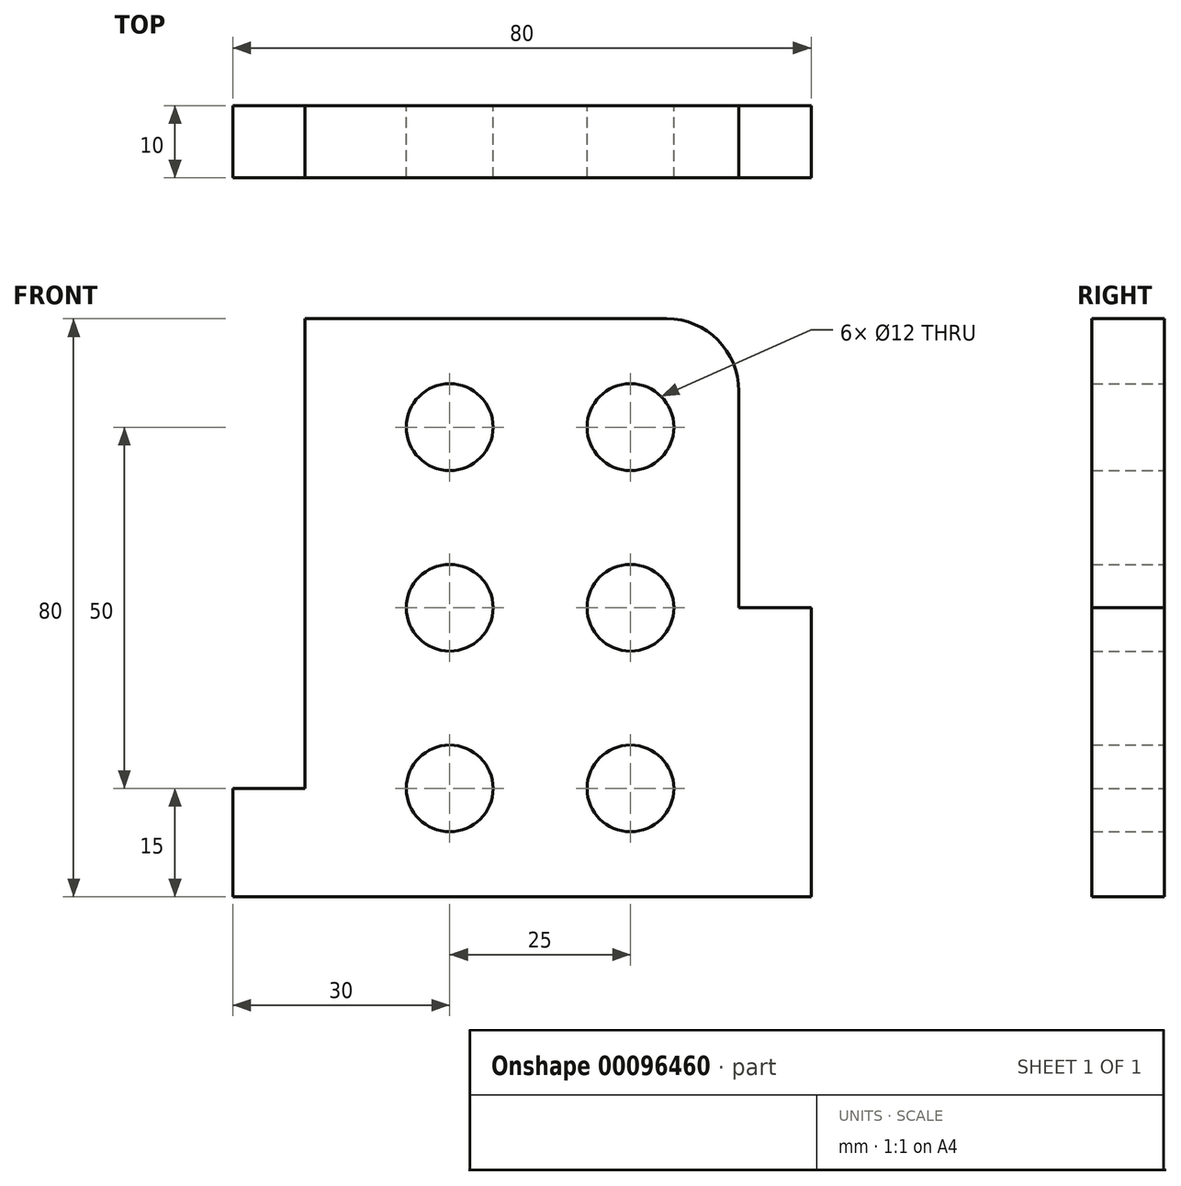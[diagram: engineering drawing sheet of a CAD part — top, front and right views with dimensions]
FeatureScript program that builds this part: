
annotation { "Feature Type Name" : "Feature", "Feature Type Description" : "" }
export const myFeature = defineFeature(function(context is Context, id is Id, definition is map)
    precondition{}
    {
        {
            var Q0;
            Q0=qCreatedBy(makeId("Front.planeOp"),FACE);
            var sketch = newSketch(context, id + "F0", { "sketchPlane" : qUnion([Q0])});
            skLineSegment(sketch, "E0", {"start": v(0, 0) * mm, "end": v(80, 0) * mm});
            skLineSegment(sketch, "E1", {"start": v(80, 0) * mm, "end": v(80, 40) * mm});
            skLineSegment(sketch, "E2", {"start": v(80, 40) * mm, "end": v(70, 40) * mm});
            skLineSegment(sketch, "E3", {"start": v(70, 40) * mm, "end": v(70, 70) * mm});
            skLineSegment(sketch, "E4", {"start": v(60, 80) * mm, "end": v(10, 80) * mm});
            skLineSegment(sketch, "E5", {"start": v(10, 80) * mm, "end": v(10, 15) * mm});
            skLineSegment(sketch, "E6", {"start": v(10, 15) * mm, "end": v(0, 15) * mm});
            skLineSegment(sketch, "E7", {"start": v(0, 15) * mm, "end": v(0, 0) * mm});
            skPoint(sketch, "E8.visualSharp", {"position": v(70, 80) * mm});
            skArc(sketch, "E8.filletArc", {"start": v(70, 70) * mm, "mid": v(67.07, 77.07) * mm, "end": v(60, 80) * mm});
            skLineSegment(sketch, "E9", {"start": v(0, 15) * mm, "end": v(30, 15) * mm, "construction": true});
            skCircle(sketch, "E10", {"center": v(30, 15) * mm, "radius": 6 * mm});
            skLineSegment(sketch, "E11", {"start": v(0, 15) * mm, "end": v(55, 15) * mm, "construction": true});
            skCircle(sketch, "E12", {"center": v(55, 15) * mm, "radius": 6 * mm});
            skLineSegment(sketch, "E13", {"start": v(70, 40) * mm, "end": v(10, 40) * mm, "construction": true});
            skLineSegment(sketch, "E14", {"start": v(30, 15) * mm, "end": v(30, 40) * mm, "construction": true});
            skLineSegment(sketch, "E15", {"start": v(55, 15) * mm, "end": v(55, 40) * mm, "construction": true});
            skCircle(sketch, "E16", {"center": v(55, 40) * mm, "radius": 6 * mm});
            skCircle(sketch, "E17", {"center": v(30, 40) * mm, "radius": 6 * mm});
            skLineSegment(sketch, "E18", {"start": v(30, 40) * mm, "end": v(30, 65) * mm, "construction": true});
            skLineSegment(sketch, "E19", {"start": v(55, 40) * mm, "end": v(55, 65) * mm, "construction": true});
            skCircle(sketch, "E20", {"center": v(30, 65) * mm, "radius": 6 * mm});
            skCircle(sketch, "E21", {"center": v(55, 65) * mm, "radius": 6 * mm});
            skSolve(sketch);
        }
        {
            var Q0;
            Q0 = qSketchRegion(id + "F0", true);
            extrude(context, id + "F1", {"entities" : qUnion([Q0]), "depth" : 10 * mm});
        }
    });
